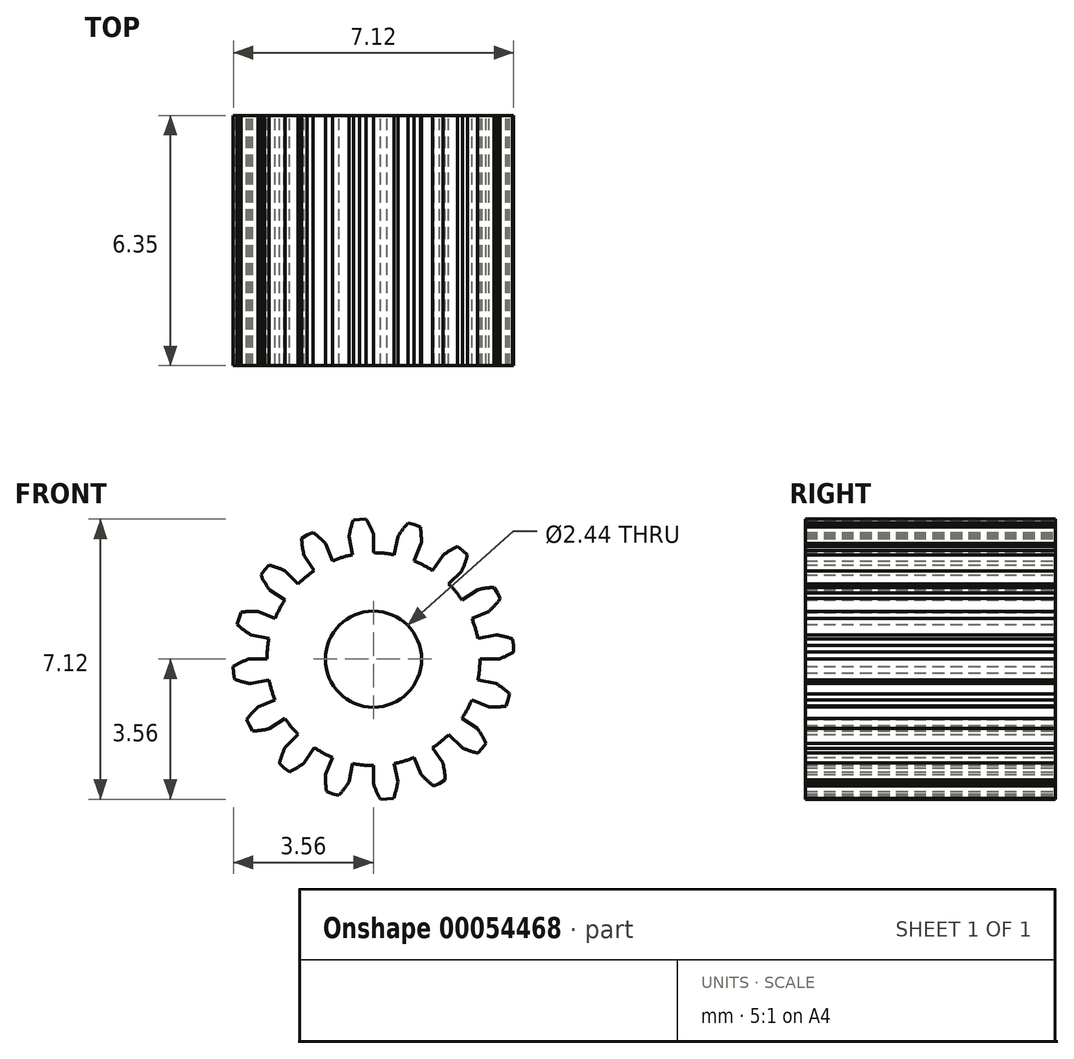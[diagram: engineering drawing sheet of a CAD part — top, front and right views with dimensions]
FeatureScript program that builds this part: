
annotation { "Feature Type Name" : "Feature", "Feature Type Description" : "" }
export const myFeature = defineFeature(function(context is Context, id is Id, definition is map)
    precondition{}
    {
        {
            var Q0;
            Q0=qCreatedBy(makeId("Front.planeOp"),FACE);
            var sketch = newSketch(context, id + "F0", { "sketchPlane" : qUnion([Q0])});
            skArc(sketch, "E0", {"start": v(-1.5, 2.25) * mm, "mid": v(-1.72, 2.1) * mm, "end": v(-1.91, 1.91) * mm});
            skArc(sketch, "E1.trimOffspring", {"start": v(0, 3.18) * mm, "mid": v(-0.08, 3.37) * mm, "end": v(-0.19, 3.56) * mm});
            skLineSegment(sketch, "E2", {"start": v(0, 3.18) * mm, "end": v(0, 2.7) * mm});
            skLineSegment(sketch, "E3", {"start": v(-0.19, 3.56) * mm, "end": v(-0.35, 3.56) * mm});
            skArc(sketch, "E4.MirrorCS", {"start": v(-0.62, 3.11) * mm, "mid": v(-0.58, 3.33) * mm, "end": v(-0.51, 3.53) * mm});
            skLineSegment(sketch, "E5.MirrorCS", {"start": v(-0.62, 3.11) * mm, "end": v(-0.53, 2.65) * mm});
            skLineSegment(sketch, "E6.MirrorCS", {"start": v(-0.51, 3.53) * mm, "end": v(-0.35, 3.56) * mm});
            skLineSegment(sketch, "E7.1.0", {"start": v(-1.22, 2.93) * mm, "end": v(-1.04, 2.5) * mm});
            skArc(sketch, "E7.1.1", {"start": v(-1.22, 2.93) * mm, "mid": v(-1.37, 3.09) * mm, "end": v(-1.54, 3.22) * mm});
            skLineSegment(sketch, "E7.1.2", {"start": v(-1.54, 3.22) * mm, "end": v(-1.68, 3.15) * mm});
            skLineSegment(sketch, "E7.1.3", {"start": v(-1.82, 3.07) * mm, "end": v(-1.68, 3.15) * mm});
            skArc(sketch, "E7.1.4", {"start": v(-1.76, 2.64) * mm, "mid": v(-1.8, 2.85) * mm, "end": v(-1.82, 3.07) * mm});
            skLineSegment(sketch, "E7.1.5", {"start": v(-1.76, 2.64) * mm, "end": v(-1.5, 2.25) * mm});
            skLineSegment(sketch, "E7.2.0", {"start": v(-2.25, 2.25) * mm, "end": v(-1.91, 1.91) * mm});
            skArc(sketch, "E7.2.1", {"start": v(-2.25, 2.25) * mm, "mid": v(-2.45, 2.33) * mm, "end": v(-2.65, 2.39) * mm});
            skLineSegment(sketch, "E7.2.2", {"start": v(-2.65, 2.39) * mm, "end": v(-2.76, 2.27) * mm});
            skLineSegment(sketch, "E7.2.3", {"start": v(-2.86, 2.14) * mm, "end": v(-2.76, 2.27) * mm});
            skArc(sketch, "E7.2.4", {"start": v(-2.64, 1.76) * mm, "mid": v(-2.76, 1.94) * mm, "end": v(-2.86, 2.14) * mm});
            skLineSegment(sketch, "E7.2.5", {"start": v(-2.64, 1.76) * mm, "end": v(-2.25, 1.5) * mm});
            skLineSegment(sketch, "E8.2.3.0", {"start": v(-2.93, 1.22) * mm, "end": v(-2.5, 1.04) * mm});
            skArc(sketch, "E8.3.3.0", {"start": v(-2.93, 1.22) * mm, "mid": v(-3.15, 1.21) * mm, "end": v(-3.36, 1.2) * mm});
            skLineSegment(sketch, "E8.7.3.0", {"start": v(-3.36, 1.2) * mm, "end": v(-3.42, 1.04) * mm});
            skLineSegment(sketch, "E8.10.3.0", {"start": v(-3.46, 0.88) * mm, "end": v(-3.42, 1.04) * mm});
            skArc(sketch, "E8.13.3.0", {"start": v(-3.11, 0.62) * mm, "mid": v(-3.3, 0.74) * mm, "end": v(-3.46, 0.88) * mm});
            skLineSegment(sketch, "E8.17.3.0", {"start": v(-3.11, 0.62) * mm, "end": v(-2.65, 0.53) * mm});
            skLineSegment(sketch, "E8.2.4.0", {"start": v(-3.18, 0) * mm, "end": v(-2.7, 0) * mm});
            skArc(sketch, "E8.3.4.0", {"start": v(-3.18, 0) * mm, "mid": v(-3.37, -0.08) * mm, "end": v(-3.56, -0.19) * mm});
            skLineSegment(sketch, "E8.7.4.0", {"start": v(-3.56, -0.19) * mm, "end": v(-3.56, -0.35) * mm});
            skLineSegment(sketch, "E8.10.4.0", {"start": v(-3.53, -0.51) * mm, "end": v(-3.56, -0.35) * mm});
            skArc(sketch, "E8.13.4.0", {"start": v(-3.11, -0.62) * mm, "mid": v(-3.33, -0.58) * mm, "end": v(-3.53, -0.51) * mm});
            skLineSegment(sketch, "E8.17.4.0", {"start": v(-3.11, -0.62) * mm, "end": v(-2.65, -0.53) * mm});
            skLineSegment(sketch, "E8.2.5.0", {"start": v(-2.93, -1.22) * mm, "end": v(-2.5, -1.04) * mm});
            skArc(sketch, "E8.3.5.0", {"start": v(-2.93, -1.22) * mm, "mid": v(-3.09, -1.37) * mm, "end": v(-3.22, -1.54) * mm});
            skLineSegment(sketch, "E8.7.5.0", {"start": v(-3.22, -1.54) * mm, "end": v(-3.15, -1.68) * mm});
            skLineSegment(sketch, "E8.10.5.0", {"start": v(-3.07, -1.82) * mm, "end": v(-3.15, -1.68) * mm});
            skArc(sketch, "E8.13.5.0", {"start": v(-2.64, -1.76) * mm, "mid": v(-2.85, -1.8) * mm, "end": v(-3.07, -1.82) * mm});
            skLineSegment(sketch, "E8.17.5.0", {"start": v(-2.64, -1.76) * mm, "end": v(-2.25, -1.5) * mm});
            skLineSegment(sketch, "E8.2.6.0", {"start": v(-2.25, -2.25) * mm, "end": v(-1.91, -1.91) * mm});
            skArc(sketch, "E8.3.6.0", {"start": v(-2.25, -2.25) * mm, "mid": v(-2.33, -2.45) * mm, "end": v(-2.39, -2.65) * mm});
            skLineSegment(sketch, "E8.7.6.0", {"start": v(-2.39, -2.65) * mm, "end": v(-2.27, -2.76) * mm});
            skLineSegment(sketch, "E8.10.6.0", {"start": v(-2.14, -2.86) * mm, "end": v(-2.27, -2.76) * mm});
            skArc(sketch, "E8.13.6.0", {"start": v(-1.76, -2.64) * mm, "mid": v(-1.94, -2.76) * mm, "end": v(-2.14, -2.86) * mm});
            skLineSegment(sketch, "E8.17.6.0", {"start": v(-1.76, -2.64) * mm, "end": v(-1.5, -2.25) * mm});
            skLineSegment(sketch, "E8.2.7.0", {"start": v(-1.22, -2.93) * mm, "end": v(-1.04, -2.5) * mm});
            skArc(sketch, "E8.3.7.0", {"start": v(-1.22, -2.93) * mm, "mid": v(-1.21, -3.15) * mm, "end": v(-1.2, -3.36) * mm});
            skLineSegment(sketch, "E8.7.7.0", {"start": v(-1.2, -3.36) * mm, "end": v(-1.04, -3.42) * mm});
            skLineSegment(sketch, "E8.10.7.0", {"start": v(-0.88, -3.46) * mm, "end": v(-1.04, -3.42) * mm});
            skArc(sketch, "E8.13.7.0", {"start": v(-0.62, -3.11) * mm, "mid": v(-0.74, -3.3) * mm, "end": v(-0.88, -3.46) * mm});
            skLineSegment(sketch, "E8.17.7.0", {"start": v(-0.62, -3.11) * mm, "end": v(-0.53, -2.65) * mm});
            skLineSegment(sketch, "E8.2.8.0", {"start": v(0, -3.18) * mm, "end": v(0, -2.7) * mm});
            skArc(sketch, "E8.3.8.0", {"start": v(0, -3.18) * mm, "mid": v(0.08, -3.37) * mm, "end": v(0.19, -3.56) * mm});
            skLineSegment(sketch, "E8.7.8.0", {"start": v(0.19, -3.56) * mm, "end": v(0.35, -3.56) * mm});
            skLineSegment(sketch, "E8.10.8.0", {"start": v(0.51, -3.53) * mm, "end": v(0.35, -3.56) * mm});
            skArc(sketch, "E8.13.8.0", {"start": v(0.62, -3.11) * mm, "mid": v(0.58, -3.33) * mm, "end": v(0.51, -3.53) * mm});
            skLineSegment(sketch, "E8.17.8.0", {"start": v(0.62, -3.11) * mm, "end": v(0.53, -2.65) * mm});
            skLineSegment(sketch, "E8.2.9.0", {"start": v(1.22, -2.93) * mm, "end": v(1.04, -2.5) * mm});
            skArc(sketch, "E8.3.9.0", {"start": v(1.22, -2.93) * mm, "mid": v(1.37, -3.09) * mm, "end": v(1.54, -3.22) * mm});
            skLineSegment(sketch, "E8.7.9.0", {"start": v(1.54, -3.22) * mm, "end": v(1.68, -3.15) * mm});
            skLineSegment(sketch, "E8.10.9.0", {"start": v(1.82, -3.07) * mm, "end": v(1.68, -3.15) * mm});
            skArc(sketch, "E8.13.9.0", {"start": v(1.76, -2.64) * mm, "mid": v(1.8, -2.85) * mm, "end": v(1.82, -3.07) * mm});
            skLineSegment(sketch, "E8.17.9.0", {"start": v(1.76, -2.64) * mm, "end": v(1.5, -2.25) * mm});
            skLineSegment(sketch, "E8.2.10.0", {"start": v(2.25, -2.25) * mm, "end": v(1.91, -1.91) * mm});
            skArc(sketch, "E8.3.10.0", {"start": v(2.25, -2.25) * mm, "mid": v(2.45, -2.33) * mm, "end": v(2.65, -2.39) * mm});
            skLineSegment(sketch, "E8.7.10.0", {"start": v(2.65, -2.39) * mm, "end": v(2.76, -2.27) * mm});
            skLineSegment(sketch, "E8.10.10.0", {"start": v(2.86, -2.14) * mm, "end": v(2.76, -2.27) * mm});
            skArc(sketch, "E8.13.10.0", {"start": v(2.64, -1.76) * mm, "mid": v(2.76, -1.94) * mm, "end": v(2.86, -2.14) * mm});
            skLineSegment(sketch, "E8.17.10.0", {"start": v(2.64, -1.76) * mm, "end": v(2.25, -1.5) * mm});
            skLineSegment(sketch, "E8.2.11.0", {"start": v(2.93, -1.22) * mm, "end": v(2.5, -1.04) * mm});
            skArc(sketch, "E8.3.11.0", {"start": v(2.93, -1.22) * mm, "mid": v(3.15, -1.21) * mm, "end": v(3.36, -1.2) * mm});
            skLineSegment(sketch, "E8.7.11.0", {"start": v(3.36, -1.2) * mm, "end": v(3.42, -1.04) * mm});
            skLineSegment(sketch, "E8.10.11.0", {"start": v(3.46, -0.88) * mm, "end": v(3.42, -1.04) * mm});
            skArc(sketch, "E8.13.11.0", {"start": v(3.11, -0.62) * mm, "mid": v(3.3, -0.74) * mm, "end": v(3.46, -0.88) * mm});
            skLineSegment(sketch, "E8.17.11.0", {"start": v(3.11, -0.62) * mm, "end": v(2.65, -0.53) * mm});
            skLineSegment(sketch, "E8.2.12.0", {"start": v(3.18, 0) * mm, "end": v(2.7, 0) * mm});
            skArc(sketch, "E8.3.12.0", {"start": v(3.18, 0) * mm, "mid": v(3.37, 0.08) * mm, "end": v(3.56, 0.19) * mm});
            skLineSegment(sketch, "E8.7.12.0", {"start": v(3.56, 0.19) * mm, "end": v(3.56, 0.35) * mm});
            skLineSegment(sketch, "E8.10.12.0", {"start": v(3.53, 0.51) * mm, "end": v(3.56, 0.35) * mm});
            skArc(sketch, "E8.13.12.0", {"start": v(3.11, 0.62) * mm, "mid": v(3.33, 0.58) * mm, "end": v(3.53, 0.51) * mm});
            skLineSegment(sketch, "E8.17.12.0", {"start": v(3.11, 0.62) * mm, "end": v(2.65, 0.53) * mm});
            skLineSegment(sketch, "E8.2.13.0", {"start": v(2.93, 1.22) * mm, "end": v(2.5, 1.04) * mm});
            skArc(sketch, "E8.3.13.0", {"start": v(2.93, 1.22) * mm, "mid": v(3.09, 1.37) * mm, "end": v(3.22, 1.54) * mm});
            skLineSegment(sketch, "E8.7.13.0", {"start": v(3.22, 1.54) * mm, "end": v(3.15, 1.68) * mm});
            skLineSegment(sketch, "E8.10.13.0", {"start": v(3.07, 1.82) * mm, "end": v(3.15, 1.68) * mm});
            skArc(sketch, "E8.13.13.0", {"start": v(2.64, 1.76) * mm, "mid": v(2.85, 1.8) * mm, "end": v(3.07, 1.82) * mm});
            skLineSegment(sketch, "E8.17.13.0", {"start": v(2.64, 1.76) * mm, "end": v(2.25, 1.5) * mm});
            skLineSegment(sketch, "E8.2.14.0", {"start": v(2.25, 2.25) * mm, "end": v(1.91, 1.91) * mm});
            skArc(sketch, "E8.3.14.0", {"start": v(2.25, 2.25) * mm, "mid": v(2.33, 2.45) * mm, "end": v(2.39, 2.65) * mm});
            skLineSegment(sketch, "E8.7.14.0", {"start": v(2.39, 2.65) * mm, "end": v(2.27, 2.76) * mm});
            skLineSegment(sketch, "E8.10.14.0", {"start": v(2.14, 2.86) * mm, "end": v(2.27, 2.76) * mm});
            skArc(sketch, "E8.13.14.0", {"start": v(1.76, 2.64) * mm, "mid": v(1.94, 2.76) * mm, "end": v(2.14, 2.86) * mm});
            skLineSegment(sketch, "E8.17.14.0", {"start": v(1.76, 2.64) * mm, "end": v(1.5, 2.25) * mm});
            skLineSegment(sketch, "E8.2.15.0", {"start": v(1.22, 2.93) * mm, "end": v(1.04, 2.5) * mm});
            skArc(sketch, "E8.3.15.0", {"start": v(1.22, 2.93) * mm, "mid": v(1.21, 3.15) * mm, "end": v(1.2, 3.36) * mm});
            skLineSegment(sketch, "E8.7.15.0", {"start": v(1.2, 3.36) * mm, "end": v(1.04, 3.42) * mm});
            skLineSegment(sketch, "E8.10.15.0", {"start": v(0.88, 3.46) * mm, "end": v(1.04, 3.42) * mm});
            skArc(sketch, "E8.13.15.0", {"start": v(0.62, 3.11) * mm, "mid": v(0.74, 3.3) * mm, "end": v(0.88, 3.46) * mm});
            skLineSegment(sketch, "E8.17.15.0", {"start": v(0.62, 3.11) * mm, "end": v(0.53, 2.65) * mm});
            skArc(sketch, "E9.trimOffspring", {"start": v(-0.53, 2.65) * mm, "mid": v(-0.79, 2.59) * mm, "end": v(-1.04, 2.5) * mm});
            skArc(sketch, "E10.trimOffspring", {"start": v(0.53, 2.65) * mm, "mid": v(0.27, 2.7) * mm, "end": v(0, 2.7) * mm});
            skArc(sketch, "E11.trimOffspring", {"start": v(1.5, 2.25) * mm, "mid": v(1.28, 2.39) * mm, "end": v(1.04, 2.5) * mm});
            skArc(sketch, "E12.trimOffspring", {"start": v(2.25, 1.5) * mm, "mid": v(2.1, 1.72) * mm, "end": v(1.91, 1.91) * mm});
            skArc(sketch, "E13.trimOffspring", {"start": v(2.65, 0.53) * mm, "mid": v(2.59, 0.79) * mm, "end": v(2.5, 1.04) * mm});
            skArc(sketch, "E14.trimOffspring", {"start": v(2.65, -0.53) * mm, "mid": v(2.7, -0.27) * mm, "end": v(2.7, 0) * mm});
            skArc(sketch, "E15.trimOffspring", {"start": v(2.25, -1.5) * mm, "mid": v(2.39, -1.28) * mm, "end": v(2.5, -1.04) * mm});
            skArc(sketch, "E16.trimOffspring", {"start": v(1.5, -2.25) * mm, "mid": v(1.72, -2.1) * mm, "end": v(1.91, -1.91) * mm});
            skArc(sketch, "E17.trimOffspring", {"start": v(0.53, -2.65) * mm, "mid": v(0.79, -2.59) * mm, "end": v(1.04, -2.5) * mm});
            skArc(sketch, "E18.trimOffspring", {"start": v(-0.53, -2.65) * mm, "mid": v(-0.27, -2.7) * mm, "end": v(0, -2.7) * mm});
            skArc(sketch, "E19.trimOffspring", {"start": v(-1.5, -2.25) * mm, "mid": v(-1.28, -2.39) * mm, "end": v(-1.04, -2.5) * mm});
            skArc(sketch, "E20.trimOffspring", {"start": v(-2.25, -1.5) * mm, "mid": v(-2.1, -1.72) * mm, "end": v(-1.91, -1.91) * mm});
            skArc(sketch, "E21.trimOffspring", {"start": v(-2.65, -0.53) * mm, "mid": v(-2.59, -0.79) * mm, "end": v(-2.5, -1.04) * mm});
            skArc(sketch, "E22.trimOffspring", {"start": v(-2.65, 0.53) * mm, "mid": v(-2.7, 0.27) * mm, "end": v(-2.7, 0) * mm});
            skArc(sketch, "E23.trimOffspring", {"start": v(-2.25, 1.5) * mm, "mid": v(-2.39, 1.28) * mm, "end": v(-2.5, 1.04) * mm});
            skSolve(sketch);
        }
        {
            var Q0;
            Q0=makeQuery(id+"F0.imprint","IMPRINT",FACE,{"disambiguationData":[TD([[makeQuery(id+"F0.imprint","IMPRINT",EDGE,{"derivedFrom":sQuery(id+"F0.wireOp",EDGE,"E0")}),1.0]])]});
            extrude(context, id + "F1", {"entities" : qUnion([Q0]), "depth" : 6.35 * mm});
        }
        {
            var Q0;
            Q0=qCreatedBy(makeId("Front.planeOp"),FACE);
            var sketch = newSketch(context, id + "F2", { "sketchPlane" : qUnion([Q0])});
            skCircle(sketch, "E24", {"center": v(0, 0) * mm, "radius": 1.22 * mm});
            skSolve(sketch);
        }
        {
            var Q0;
            Q0=makeQuery(id+"F2.imprint","IMPRINT",FACE,{"disambiguationData":[TD([[makeQuery(id+"F2.imprint","IMPRINT",EDGE,{"derivedFrom":sQuery(id+"F2.wireOp",EDGE,"E24")}),1.0]])]});
            extrude(context, id + "F3", {"entities" : qUnion([Q0]), "operationType" : NewBodyOperationType.REMOVE, "depth" : 30.9 * mm});
        }
    });
